# Revit family: QF_ZANUSSI_644213_AMPV1116DT
name_source: partatom
category: Specialty Equipment
units: mm (PartAtom-declared; Revit-internal decimal feet)

## family parameters
Always vertical = Yes
Cut with Voids When Loaded = No
Enable Cutting in Views = No
Maintain Annotation Orientation = No
Part Type = Normal
Room Calculation Point = No
Round Connector Dimension = Use Diameter
Shared = No
Work Plane-Based = No

## types (1)
- QF_ZANUSSI_644213_AMPV1116DT
    Accessory = No
    Cycle = 50 Hz
    Default Elevation = 0 mm  [stored 0 ft]
    Depth Actual = 1100 mm
    Description = 304 S/S WALL HOOD+FILTERS+FAN 1600X1100
    Gas KW = 0
    HP = 0.4 HP
    Height Actual = 500 mm  [stored 1.64042 ft]
    Item Number = 644213
    Length Actual = 1600 mm  [stored 5.24934 ft]
    Manufacturer = Zanussi
    Model = AMPV1116DT
    Phase = 1
    URL = http://www.zanussiprofessional.com
    URL Manufacturer = http://www.zanussiprofessional.com
    Volts = 220 V
    Watts = 0 W
    Weight = 51.00 kg

note: [stored X ft] marks values corroborated as IEEE doubles in the binary element streams (Revit-internal decimal feet)

## geometry (parser evidence)
native form markers: Sweep x2
no freeform markers — native parametric forms only
